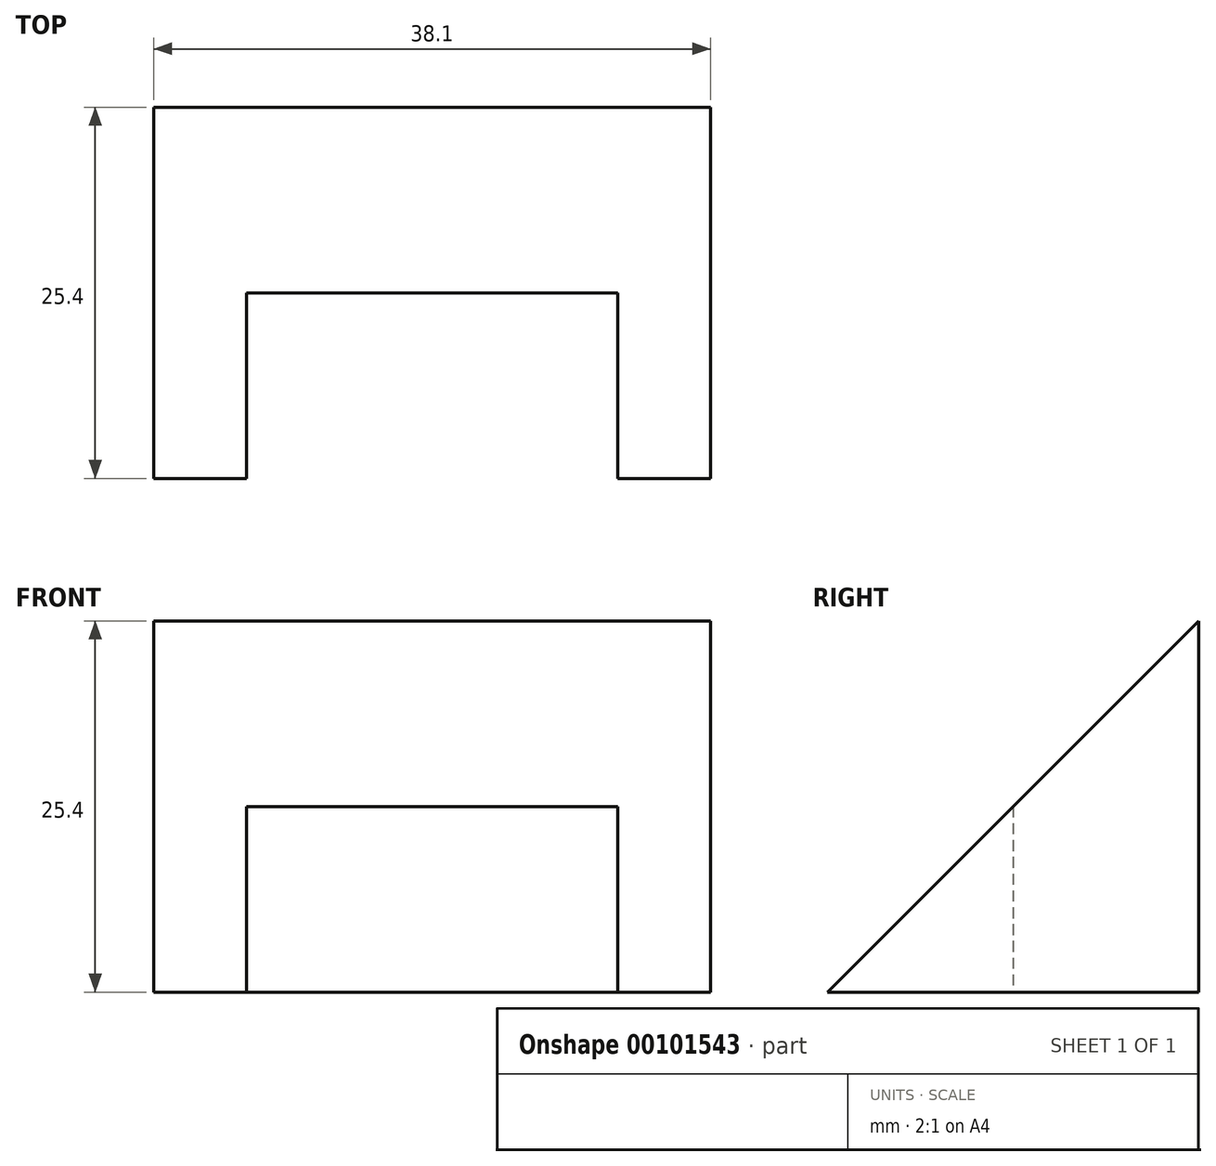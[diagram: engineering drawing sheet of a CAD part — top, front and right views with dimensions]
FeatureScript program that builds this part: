
annotation { "Feature Type Name" : "Feature", "Feature Type Description" : "" }
export const myFeature = defineFeature(function(context is Context, id is Id, definition is map)
    precondition{}
    {
        {
            var Q0;
            Q0=qCreatedBy(makeId("Right.planeOp"),FACE);
            var sketch = newSketch(context, id + "F0", { "sketchPlane" : qUnion([Q0])});
            skLineSegment(sketch, "E0", {"start": v(0, 0) * mm, "end": v(25.4, 0) * mm});
            skLineSegment(sketch, "E1", {"start": v(25.4, 0) * mm, "end": v(25.4, 25.4) * mm});
            skLineSegment(sketch, "E2", {"start": v(25.4, 25.4) * mm, "end": v(0, 0) * mm});
            skSolve(sketch);
        }
        {
            var Q0;
            Q0=makeQuery(id+"F0.imprint","IMPRINT",FACE,{"disambiguationData":[TD([[makeQuery(id+"F0.imprint","IMPRINT",EDGE,{"derivedFrom":sQuery(id+"F0.wireOp",EDGE,"E0")}),1.0]])]});
            extrude(context, id + "F1", {"entities" : qUnion([Q0]), "oppositeDirection" : true, "depth" : 38.1 * mm});
        }
        {
            var Q0;
            Q0=makeQuery(id+"F1.opExtrude","SWEPT_FACE",FACE,{"disambiguationData":[OSD([sQuery(id+"F0.wireOp",EDGE,"E0")])]});
            var sketch = newSketch(context, id + "F2", { "sketchPlane" : qUnion([Q0])});
            skLineSegment(sketch, "E3", {"start": v(-6.35, 0) * mm, "end": v(-6.35, -12.7) * mm});
            skLineSegment(sketch, "E4", {"start": v(-6.35, -12.7) * mm, "end": v(-31.75, -12.7) * mm});
            skLineSegment(sketch, "E5", {"start": v(-31.75, -12.7) * mm, "end": v(-31.75, 0) * mm});
            skSolve(sketch);
        }
        {
            var Q0;
            {var subQ0=sQuery(id+"F2.wireOp",EDGE,"E3");Q0=makeQuery(id+"F2.imprint","IMPRINT",FACE,{"disambiguationData":[TD([[makeQuery(id+"F2.imprint","IMPRINT",EDGE,{"derivedFrom":subQ0}),-1.0]])]});}
            extrude(context, id + "F3", {"entities" : qUnion([Q0]), "operationType" : NewBodyOperationType.REMOVE, "endBound" : BoundingType.THROUGH_ALL, "oppositeDirection" : true, "depth" : 25.4 * mm});
        }
    });
